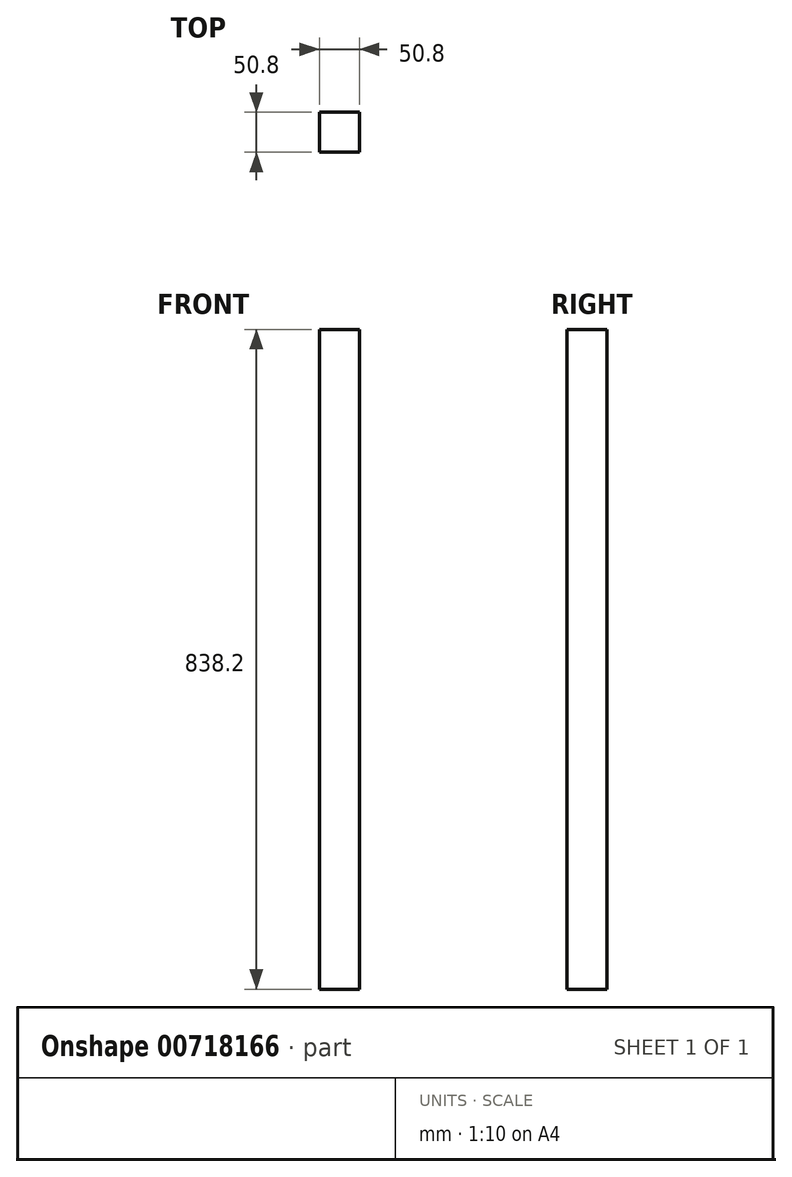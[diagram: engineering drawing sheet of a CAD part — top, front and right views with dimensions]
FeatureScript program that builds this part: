
annotation { "Feature Type Name" : "Feature", "Feature Type Description" : "" }
export const myFeature = defineFeature(function(context is Context, id is Id, definition is map)
    precondition{}
    {
        {
            var Q0;
            Q0=qCreatedBy(makeId("Top.planeOp"),FACE);
            var sketch = newSketch(context, id + "F0", { "sketchPlane" : qUnion([Q0])});
            skLineSegment(sketch, "E0.bottom", {"start": v(0, 0) * mm, "end": v(50.8, 0) * mm});
            skLineSegment(sketch, "E0.top", {"start": v(0, 50.8) * mm, "end": v(50.8, 50.8) * mm});
            skLineSegment(sketch, "E0.left", {"start": v(0, 0) * mm, "end": v(0, 50.8) * mm});
            skLineSegment(sketch, "E0.right", {"start": v(50.8, 0) * mm, "end": v(50.8, 50.8) * mm});
            skSolve(sketch);
        }
        {
            var Q0;
            Q0 = qSketchRegion(id + "F0", true);
            extrude(context, id + "F1", {"entities" : qUnion([Q0]), "depth" : 838.2 * mm, "offsetDistance" : 25.4 * mm});
        }
    });
